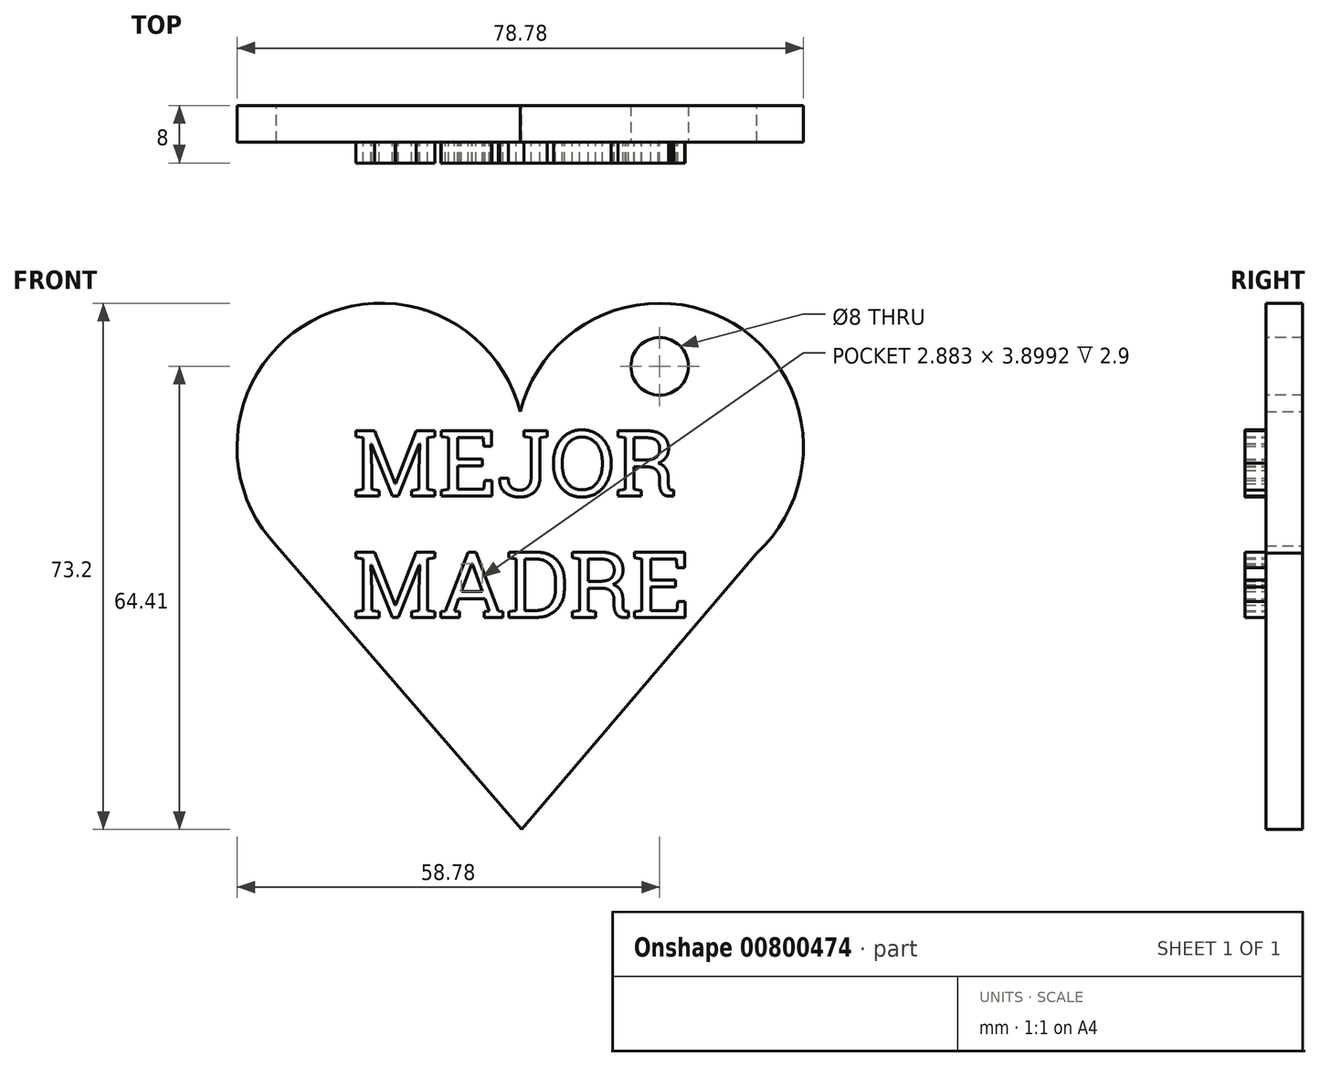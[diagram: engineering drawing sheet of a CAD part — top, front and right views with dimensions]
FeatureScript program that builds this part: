
annotation { "Feature Type Name" : "Feature", "Feature Type Description" : "" }
export const myFeature = defineFeature(function(context is Context, id is Id, definition is map)
    precondition{}
    {
        {
            var Q0;
            Q0=qCreatedBy(makeId("Front.planeOp"),FACE);
            var sketch = newSketch(context, id + "F0", { "sketchPlane" : qUnion([Q0])});
            skCircle(sketch, "E0", {"center": v(0, 0) * mm, "radius": 20 * mm});
            skCircle(sketch, "E1", {"center": v(-38.78, 0) * mm, "radius": 20 * mm});
            skLineSegment(sketch, "E2", {"start": v(-19.19, -53.2) * mm, "end": v(16.74, -10.95) * mm});
            skLineSegment(sketch, "E3", {"start": v(-53.31, -13.74) * mm, "end": v(-19.19, -53.2) * mm});
            skSolve(sketch);
        }
        {
            var Q0;
            Q0 = qSketchRegion(id + "F0", true);
            extrude(context, id + "F1", {"entities" : qUnion([Q0]), "depth" : 5.1 * mm, "offsetDistance" : 25 * mm});
        }
        {
            var Q0;
            Q0=qCreatedBy(makeId("Front.planeOp"),FACE);
            var sketch = newSketch(context, id + "F2", { "sketchPlane" : qUnion([Q0])});
            skText(sketch, "E4", { "text": "MEJOR \nMADRE", "fontName": "RobotoSlab-Regular.ttf"});
            const initialGuessF2  = {"E4": [-0.04269, -0.00683, 1, 0, 0.0092]};
            skSetInitialGuess(sketch, initialGuessF2);
            skSolve(sketch);
        }
        {
            var Q0;
            Q0 = qSketchRegion(id + "F2", true);
            extrude(context, id + "F3", {"entities" : qUnion([Q0]), "operationType" : NewBodyOperationType.ADD, "depth" : 8 * mm, "offsetDistance" : 25 * mm});
        }
        {
            var Q0;
            Q0=qCreatedBy(makeId("Front.planeOp"),FACE);
            var sketch = newSketch(context, id + "F4", { "sketchPlane" : qUnion([Q0])});
            skCircle(sketch, "E5", {"center": v(0, 11) * mm, "radius": 7 * mm});
            skSolve(sketch);
        }
        {
            var Q0;
            Q0 = qSketchRegion(id + "F4", true);
            extrude(context, id + "F5", {"entities" : qUnion([Q0]), "operationType" : NewBodyOperationType.ADD, "depth" : 5 * mm, "offsetDistance" : 25 * mm});
        }
        {
            var Q0;
            Q0=qCreatedBy(makeId("Front.planeOp"),FACE);
            var sketch = newSketch(context, id + "F6", { "sketchPlane" : qUnion([Q0])});
            skCircle(sketch, "E6", {"center": v(0, 11.21) * mm, "radius": 4 * mm});
            skSolve(sketch);
        }
        {
            var Q0;
            Q0 = qSketchRegion(id + "F6", true);
            extrude(context, id + "F7", {"entities" : qUnion([Q0]), "operationType" : NewBodyOperationType.REMOVE, "oppositeDirection" : true, "depth" : 25 * mm, "offsetDistance" : 25 * mm, "hasSecondDirection" : true, "secondDirectionOppositeDirection" : false, "secondDirectionDepth" : 25 * mm});
        }
    });
